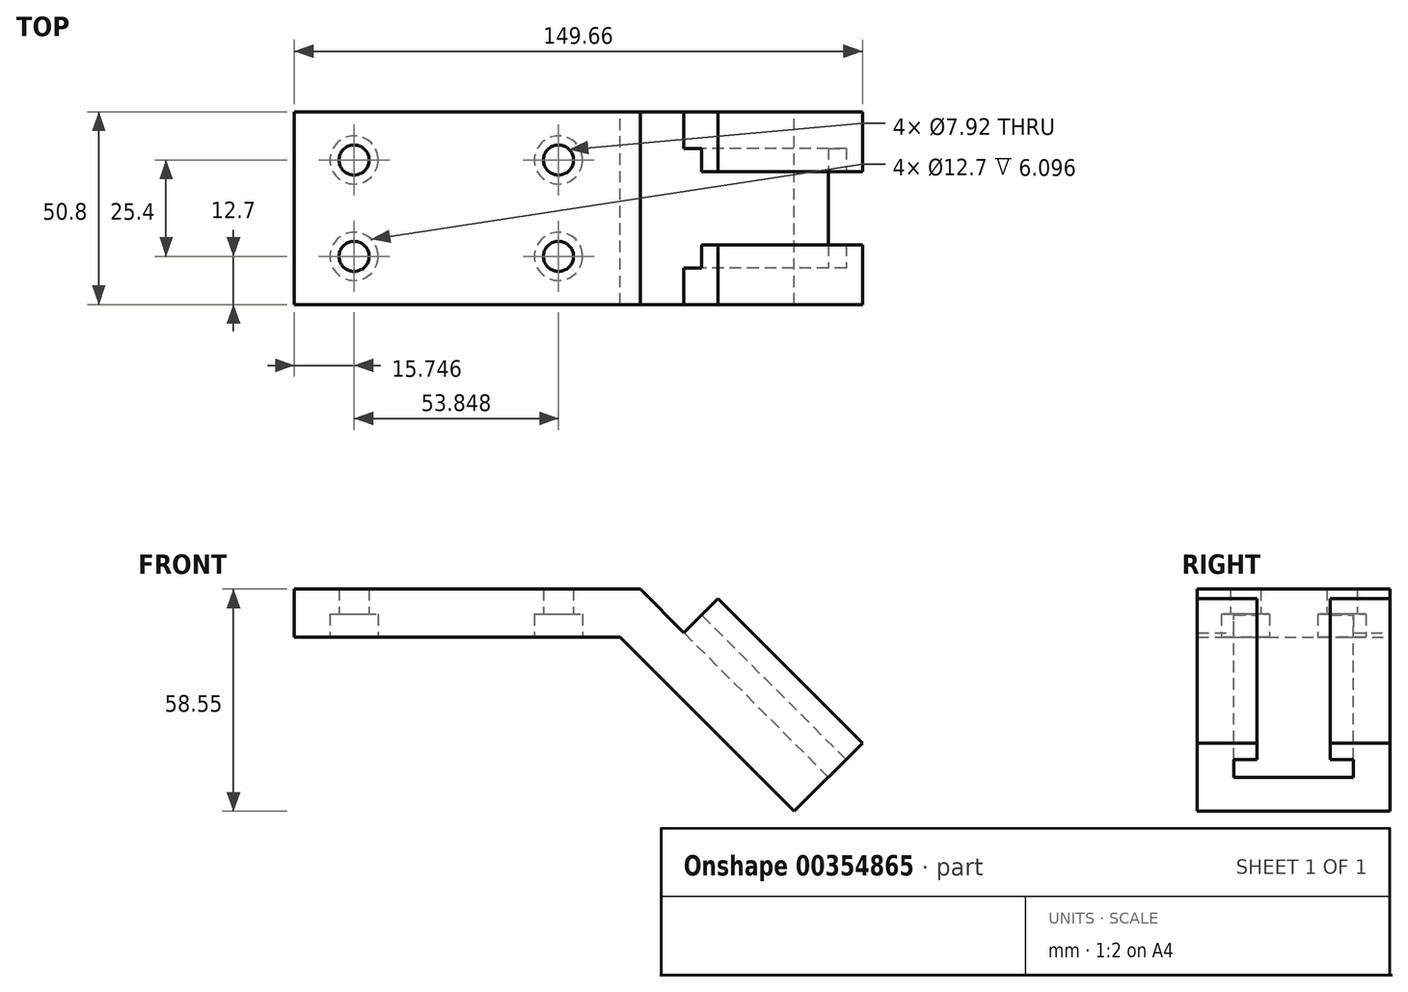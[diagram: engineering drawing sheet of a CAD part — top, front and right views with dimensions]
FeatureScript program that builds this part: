
annotation { "Feature Type Name" : "Feature", "Feature Type Description" : "" }
export const myFeature = defineFeature(function(context is Context, id is Id, definition is map)
    precondition{}
    {
        {
            var Q0;
            Q0=qCreatedBy(makeId("Front.planeOp"),FACE);
            var sketch = newSketch(context, id + "F0", { "sketchPlane" : qUnion([Q0])});
            skLineSegment(sketch, "E0", {"start": v(-85.85, 0) * mm, "end": v(-85.85, 12.7) * mm});
            skLineSegment(sketch, "E1", {"start": v(-85.85, 12.7) * mm, "end": v(5.26, 12.7) * mm});
            skLineSegment(sketch, "E2", {"start": v(5.26, 12.7) * mm, "end": v(16.76, 1.2) * mm});
            skLineSegment(sketch, "E3", {"start": v(16.76, 1.2) * mm, "end": v(25.74, 10.19) * mm});
            skLineSegment(sketch, "E4", {"start": v(25.74, 10.19) * mm, "end": v(63.81, -27.9) * mm});
            skLineSegment(sketch, "E5", {"start": v(63.81, -27.9) * mm, "end": v(45.85, -45.85) * mm});
            skLineSegment(sketch, "E6", {"start": v(45.85, -45.85) * mm, "end": v(0, 0) * mm});
            skLineSegment(sketch, "E7", {"start": v(0, 0) * mm, "end": v(-85.85, 0) * mm});
            skSolve(sketch);
        }
        {
            var Q0;
            Q0 = qSketchRegion(id + "F0", true);
            extrude(context, id + "F1", {"entities" : qUnion([Q0]), "endBound" : BoundingType.SYMMETRIC, "depth" : 50.8 * mm});
        }
        {
            var Q0;
            Q0=makeQuery(id+"F1.opExtrude","SWEPT_FACE",FACE,{"disambiguationData":[OSD([sQuery(id+"F0.wireOp",EDGE,"E7")])]});
            var sketch = newSketch(context, id + "F2", { "sketchPlane" : qUnion([Q0])});
            skPoint(sketch, "E8", {"position": v(-70.1, 12.7) * mm});
            skPoint(sketch, "E9", {"position": v(-70.1, -12.7) * mm});
            skPoint(sketch, "E10", {"position": v(-16.26, -12.7) * mm});
            skPoint(sketch, "E11", {"position": v(-16.26, 12.7) * mm});
            skSolve(sketch);
        }
        {
            var Q0;
            Q0=sQuery(id+"F2.wireOp",VERTEX,"E8");
            var Q1;
            Q1=sQuery(id+"F2.wireOp",VERTEX,"E11");
            var Q2;
            Q2=sQuery(id+"F2.wireOp",VERTEX,"E9");
            var Q3;
            Q3=sQuery(id+"F2.wireOp",VERTEX,"E10");
            var Q4;
            Q4=makeQuery(id+"F1.opExtrude","SWEPT_BODY",BODY,{"disambiguationData":[OSD([sQuery(id+"F0.wireOp",EDGE,"E0"),sQuery(id+"F0.wireOp",EDGE,"E1"),sQuery(id+"F0.wireOp",EDGE,"E2"),sQuery(id+"F0.wireOp",EDGE,"E3"),sQuery(id+"F0.wireOp",EDGE,"E4"),sQuery(id+"F0.wireOp",EDGE,"E5"),sQuery(id+"F0.wireOp",EDGE,"E6"),sQuery(id+"F0.wireOp",EDGE,"E7")])]});
            hole(context, id + "F3", {"style" : HoleStyle.C_BORE, "endStyle" : HoleEndStyle.THROUGH, "holeDiameter" : 7.92 * mm, "cBoreDiameter" : 12.7 * mm, "cBoreDepth" : 6.1 * mm, "isTappedThrough" : true, "tappedDepth" : 12.7 * mm, "tapClearance" : 3, "locations" : qUnion([Q0, Q1, Q2, Q3]), "scope" : qUnion([Q4])});
        }
        {
            var Q0;
            Q0=makeQuery(id+"F1.opExtrude","SWEPT_FACE",FACE,{"disambiguationData":[OSD([sQuery(id+"F0.wireOp",EDGE,"E4")])]});
            var sketch = newSketch(context, id + "F4", { "sketchPlane" : qUnion([Q0])});
            skArc(sketch, "E12", {"start": v(58.48, -25.4) * mm, "mid": v(64.84, 0) * mm, "end": v(58.48, 25.4) * mm});
            skLineSegment(sketch, "E13", {"start": v(58.48, 25.4) * mm, "end": v(64.84, 25.4) * mm});
            skLineSegment(sketch, "E14", {"start": v(64.84, 25.4) * mm, "end": v(64.84, -25.4) * mm});
            skLineSegment(sketch, "E15", {"start": v(64.84, -25.4) * mm, "end": v(58.48, -25.4) * mm});
            skSolve(sketch);
        }
        {
            var Q0;
            Q0 = qSketchRegion(id + "F4", true);
            extrude(context, id + "F5", {"entities" : qUnion([Q0]), "operationType" : NewBodyOperationType.REMOVE, "oppositeDirection" : true, "depth" : 25.4 * mm});
        }
        {
            var Q0;
            Q0=makeQuery(id+"F1.opExtrude","SWEPT_FACE",FACE,{"disambiguationData":[OSD([sQuery(id+"F0.wireOp",EDGE,"E3")])]});
            var sketch = newSketch(context, id + "F6", { "sketchPlane" : qUnion([Q0])});
            skLineSegment(sketch, "E16", {"start": v(-9.65, 25.4) * mm, "end": v(-9.65, 19.3) * mm});
            skLineSegment(sketch, "E17", {"start": v(-9.65, 19.3) * mm, "end": v(-15.75, 19.3) * mm});
            skLineSegment(sketch, "E18", {"start": v(-15.75, 19.3) * mm, "end": v(-15.75, 12.7) * mm});
            skLineSegment(sketch, "E19", {"start": v(-15.75, 12.7) * mm, "end": v(15.75, 12.7) * mm});
            skLineSegment(sketch, "E20", {"start": v(15.75, 12.7) * mm, "end": v(15.75, 19.3) * mm});
            skLineSegment(sketch, "E21", {"start": v(15.75, 19.3) * mm, "end": v(9.65, 19.3) * mm});
            skLineSegment(sketch, "E22", {"start": v(9.65, 19.3) * mm, "end": v(9.65, 25.4) * mm});
            skLineSegment(sketch, "E23", {"start": v(9.65, 25.4) * mm, "end": v(-9.65, 25.4) * mm});
            skSolve(sketch);
        }
        {
            var Q0;
            Q0 = qSketchRegion(id + "F6", true);
            extrude(context, id + "F7", {"entities" : qUnion([Q0]), "operationType" : NewBodyOperationType.REMOVE, "endBound" : BoundingType.THROUGH_ALL, "oppositeDirection" : true, "depth" : 25.4 * mm});
        }
    });
